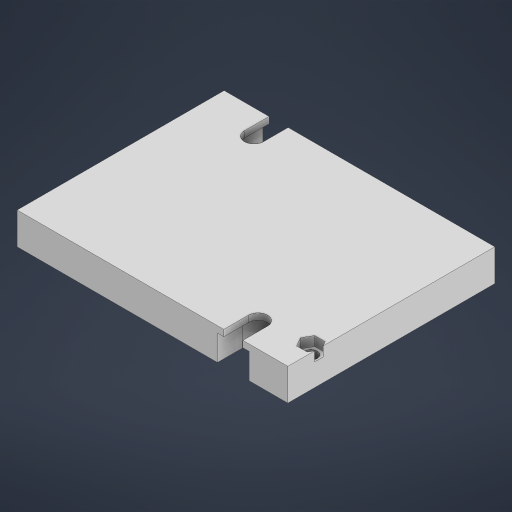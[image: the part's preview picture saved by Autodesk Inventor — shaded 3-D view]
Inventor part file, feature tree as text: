
AUTODESK INVENTOR PART (.ipt)
format: ipt  version: 2023 (Build 270158000, 158)  size: 507,392 bytes
history: native  units: mm
features: extrude x5, sketch x3, projected_geometry x1
ambient origin geometry x8: Origin, YZ Plane, XZ Plane, XY Plane, X Axis, Y Axis, Z Axis, Center Point
bodies: Solid1 (feature_tree)
feature tree (9):
  sketch  "Sketch1"  dims[d2=50.8mm d3=49.53mm]
  sketch  "Sketch2"  dims[d4=6.0mm d5=10.0mm]
  extrude  "Extrusion1"  Depth=50.8mm
  extrude  "Extrusion2"  Depth=10.0mm
  extrude  "Extrusion3"  Depth=3.0mm
  extrude  "Extrusion4"  Depth=3.0mm
  extrude  "Extrusion5"  Depth=3.0mm
  sketch  "Sketch3"  dims[d6=86.0mm d7=58.5mm d8=2.8mm d9=3.0mm d10=2.0mm d11=4.0mm d12=5.0mm d13=4.5mm d14=10.0mm d15=0.0mm d16=8.0mm d17=0.0mm d18=5.0mm d19=0.0mm d20=0.0mm d21=0.0mm d22=5.7mm d23=3.0mm d24=0.0mm]
  projected_geometry  "Projected Loop1"
